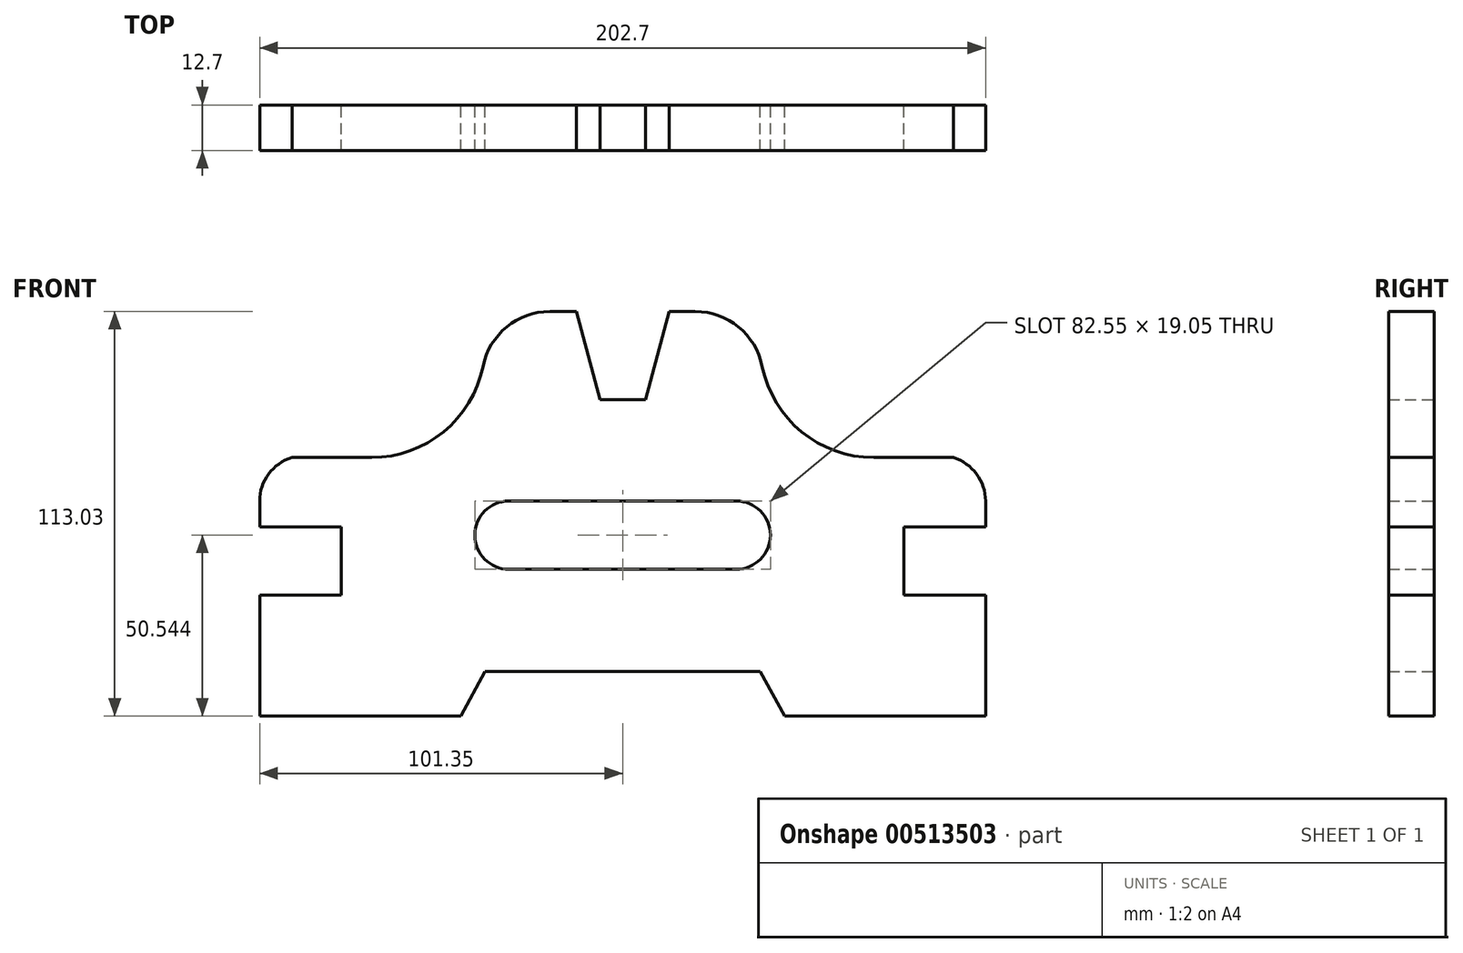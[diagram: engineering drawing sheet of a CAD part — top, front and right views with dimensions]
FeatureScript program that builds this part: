
annotation { "Feature Type Name" : "Feature", "Feature Type Description" : "" }
export const myFeature = defineFeature(function(context is Context, id is Id, definition is map)
    precondition{}
    {
        {
            var Q0;
            Q0=qCreatedBy(makeId("Front.planeOp"),FACE);
            var sketch = newSketch(context, id + "F0", { "sketchPlane" : qUnion([Q0])});
            skLineSegment(sketch, "E0", {"start": v(-78.57, 19.05) * mm, "end": v(-78.57, 0) * mm});
            skLineSegment(sketch, "E1", {"start": v(-78.57, 0) * mm, "end": v(-101.35, 0) * mm});
            skLineSegment(sketch, "E2", {"start": v(-101.35, 0) * mm, "end": v(-101.35, -33.78) * mm});
            skLineSegment(sketch, "E3", {"start": v(-101.35, -33.78) * mm, "end": v(-45.21, -33.78) * mm});
            skLineSegment(sketch, "E4", {"start": v(-45.21, -33.78) * mm, "end": v(-38.45, -21.34) * mm});
            skLineSegment(sketch, "E5", {"start": v(-38.45, -21.34) * mm, "end": v(38.63, -21.34) * mm});
            skLineSegment(sketch, "E6", {"start": v(-78.57, 19.05) * mm, "end": v(-101.35, 19.05) * mm});
            skLineSegment(sketch, "E7", {"start": v(-101.35, 19.05) * mm, "end": v(-101.35, 26.29) * mm});
            skArc(sketch, "E8", {"start": v(-101.35, 26.29) * mm, "mid": v(-98.84, 33.85) * mm, "end": v(-92.33, 38.44) * mm});
            skLineSegment(sketch, "E9", {"start": v(-92.33, 38.44) * mm, "end": v(-70.1, 38.44) * mm});
            skArc(sketch, "E10", {"start": v(-70.1, 38.44) * mm, "mid": v(-49.98, 45.63) * mm, "end": v(-38.97, 63.95) * mm});
            skArc(sketch, "E11", {"start": v(-38.97, 63.95) * mm, "mid": v(-32.37, 74.93) * mm, "end": v(-20.3, 79.25) * mm});
            skLineSegment(sketch, "E12", {"start": v(-20.3, 79.25) * mm, "end": v(-12.95, 79.25) * mm});
            skLineSegment(sketch, "E13", {"start": v(-12.95, 79.25) * mm, "end": v(-6.35, 54.6) * mm});
            skLineSegment(sketch, "E14", {"start": v(0, 75.28) * mm, "end": v(0, -51.66) * mm, "construction": true});
            skLineSegment(sketch, "E15.MirrorCS", {"start": v(12.95, 79.25) * mm, "end": v(6.35, 54.6) * mm});
            skLineSegment(sketch, "E16.MirrorCS", {"start": v(20.3, 79.25) * mm, "end": v(12.95, 79.25) * mm});
            skArc(sketch, "E17.MirrorCS", {"start": v(38.97, 63.95) * mm, "mid": v(32.37, 74.93) * mm, "end": v(20.3, 79.25) * mm});
            skArc(sketch, "E18.MirrorCS", {"start": v(70.1, 38.44) * mm, "mid": v(49.98, 45.63) * mm, "end": v(38.97, 63.95) * mm});
            skLineSegment(sketch, "E19.MirrorCS", {"start": v(92.33, 38.44) * mm, "end": v(70.1, 38.44) * mm});
            skArc(sketch, "E20.MirrorCS", {"start": v(101.35, 26.29) * mm, "mid": v(98.84, 33.85) * mm, "end": v(92.33, 38.44) * mm});
            skLineSegment(sketch, "E21.MirrorCS", {"start": v(101.35, 19.05) * mm, "end": v(101.35, 26.29) * mm});
            skLineSegment(sketch, "E22.MirrorCS", {"start": v(78.57, 19.05) * mm, "end": v(101.35, 19.05) * mm});
            skLineSegment(sketch, "E23.MirrorCS", {"start": v(78.57, 19.05) * mm, "end": v(78.57, 0) * mm});
            skLineSegment(sketch, "E24.MirrorCS", {"start": v(78.57, 0) * mm, "end": v(101.35, 0) * mm});
            skLineSegment(sketch, "E25.MirrorCS", {"start": v(101.35, 0) * mm, "end": v(101.35, -33.78) * mm});
            skLineSegment(sketch, "E26.MirrorCS", {"start": v(101.35, -33.78) * mm, "end": v(45.21, -33.78) * mm});
            skLineSegment(sketch, "E27.MirrorCS", {"start": v(45.21, -33.78) * mm, "end": v(38.45, -21.34) * mm});
            skLineSegment(sketch, "E28", {"start": v(-6.35, 54.6) * mm, "end": v(6.35, 54.6) * mm});
            skLineSegment(sketch, "E29", {"start": v(6.35, 54.6) * mm, "end": v(6.35, 73.91) * mm, "construction": true});
            skLineSegment(sketch, "E30", {"start": v(-31.75, 26.29) * mm, "end": v(31.75, 26.29) * mm});
            skLineSegment(sketch, "E31", {"start": v(-31.75, 7.24) * mm, "end": v(31.75, 7.24) * mm});
            skArc(sketch, "E32", {"start": v(-31.75, 26.29) * mm, "mid": v(-41.27, 16.76) * mm, "end": v(-31.75, 7.24) * mm});
            skArc(sketch, "E33", {"start": v(31.75, 26.29) * mm, "mid": v(41.28, 16.76) * mm, "end": v(31.75, 7.24) * mm});
            skSolve(sketch);
        }
        {
            var Q0;
            Q0=makeQuery(id+"F0.imprint","IMPRINT",FACE,{"disambiguationData":[TD([[makeQuery(id+"F0.imprint","IMPRINT",EDGE,{"derivedFrom":sQuery(id+"F0.wireOp",EDGE,"E0")}),1.0]])]});
            extrude(context, id + "F1", {"entities" : qUnion([Q0]), "endBound" : BoundingType.SYMMETRIC, "depth" : 12.7 * mm, "offsetDistance" : 25.4 * mm});
        }
    });
